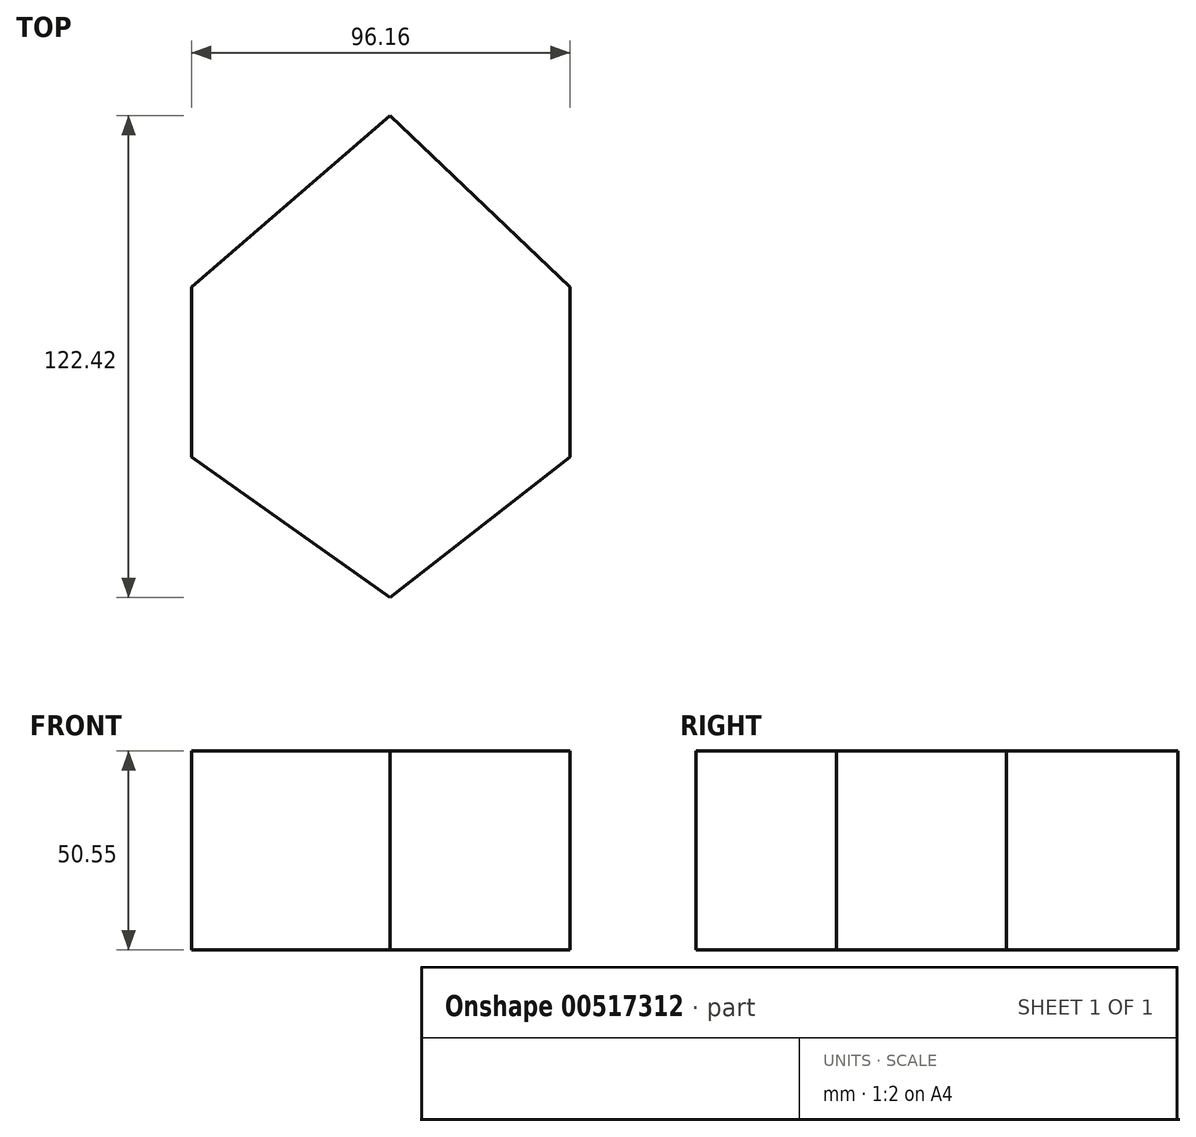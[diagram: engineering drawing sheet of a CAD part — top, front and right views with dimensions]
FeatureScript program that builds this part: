
annotation { "Feature Type Name" : "Feature", "Feature Type Description" : "" }
export const myFeature = defineFeature(function(context is Context, id is Id, definition is map)
    precondition{}
    {
        {
            var Q0;
            Q0=qCreatedBy(makeId("Top.planeOp"),FACE);
            var sketch = newSketch(context, id + "F0", { "sketchPlane" : qUnion([Q0])});
            skLineSegment(sketch, "E0", {"start": v(-50.37, 3.37) * mm, "end": v(0, 47) * mm});
            skLineSegment(sketch, "E1", {"start": v(0, 47) * mm, "end": v(45.79, 3.37) * mm});
            skLineSegment(sketch, "E2", {"start": v(45.79, 3.37) * mm, "end": v(45.79, -39.76) * mm});
            skLineSegment(sketch, "E3", {"start": v(45.79, -39.76) * mm, "end": v(0, -75.43) * mm});
            skLineSegment(sketch, "E4", {"start": v(0, -75.43) * mm, "end": v(-50.37, -39.76) * mm});
            skLineSegment(sketch, "E5", {"start": v(-50.37, -39.76) * mm, "end": v(-50.37, 3.37) * mm});
            skSolve(sketch);
        }
        {
            var Q0;
            Q0=makeQuery(id+"F0.imprint","IMPRINT",FACE,{"disambiguationData":[TD([[makeQuery(id+"F0.imprint","IMPRINT",EDGE,{"derivedFrom":sQuery(id+"F0.wireOp",EDGE,"E0")}),-1.0]])]});
            extrude(context, id + "F1", {"entities" : qUnion([Q0]), "depth" : 50.55 * mm, "offsetDistance" : 25.4 * mm});
        }
    });
